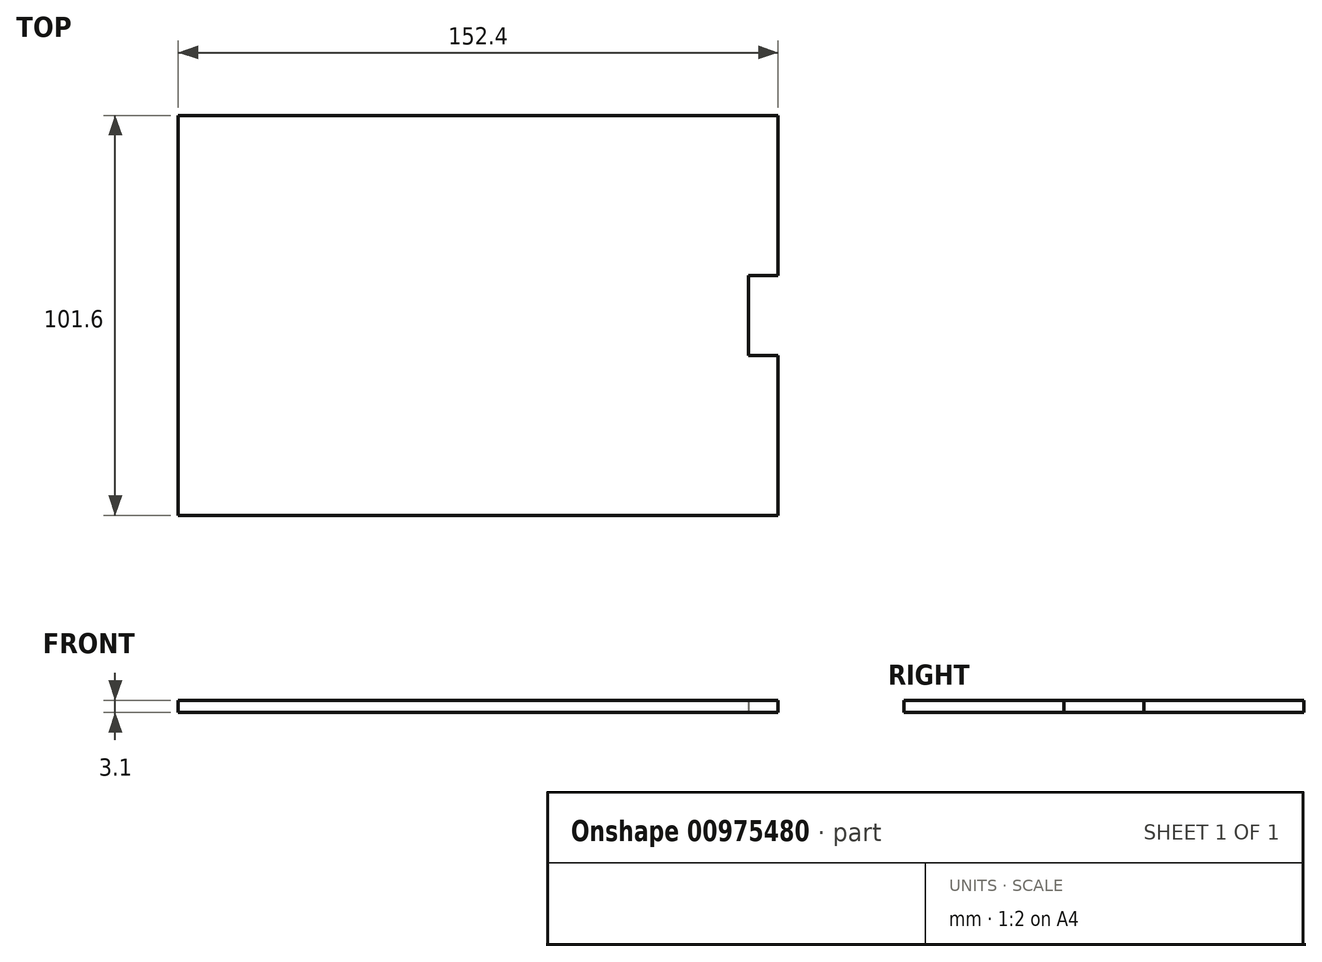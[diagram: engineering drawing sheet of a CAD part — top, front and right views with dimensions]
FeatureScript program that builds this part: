
annotation { "Feature Type Name" : "Feature", "Feature Type Description" : "" }
export const myFeature = defineFeature(function(context is Context, id is Id, definition is map)
    precondition{}
    {
        {
            var Q0;
            Q0=qCreatedBy(makeId("Top.planeOp"),FACE);
            var sketch = newSketch(context, id + "F0", { "sketchPlane" : qUnion([Q0])});
            skLineSegment(sketch, "E0.bottom", {"start": v(0, 0) * mm, "end": v(152.4, 0) * mm});
            skLineSegment(sketch, "E0.top", {"start": v(0, 101.6) * mm, "end": v(152.4, 101.6) * mm});
            skLineSegment(sketch, "E0.left", {"start": v(0, 0) * mm, "end": v(0, 101.6) * mm});
            skLineSegment(sketch, "E0.right", {"start": v(152.4, 0) * mm, "end": v(152.4, 101.6) * mm});
            skLineSegment(sketch, "E1.left", {"start": v(152.4, 60.96) * mm, "end": v(152.4, 40.64) * mm});
            skLineSegment(sketch, "E2", {"start": v(152.4, 50.8) * mm, "end": v(127.68, 50.8) * mm, "construction": true});
            skLineSegment(sketch, "E3.bottom", {"start": v(152.4, 60.96) * mm, "end": v(144.89, 60.96) * mm});
            skLineSegment(sketch, "E3.top", {"start": v(152.4, 40.64) * mm, "end": v(144.89, 40.64) * mm});
            skLineSegment(sketch, "E3.right", {"start": v(144.89, 60.96) * mm, "end": v(144.89, 40.64) * mm});
            skSolve(sketch);
        }
        {
            var Q0;
            Q0=makeQuery(id+"F0.imprint","IMPRINT",FACE,{"disambiguationData":[TD([[makeQuery(id+"F0.imprint","IMPRINT",EDGE,{"derivedFrom":sQuery(id+"F0.wireOp",EDGE,"E0.bottom")}),1.0]])]});
            var Q1;
            Q1=makeQuery(id+"F0.imprint","IMPRINT",FACE,{"disambiguationData":[TD([[makeQuery(id+"F0.imprint","IMPRINT",EDGE,{"derivedFrom":sQuery(id+"F0.wireOp",EDGE,"E1.bottom")}),-1.0]])]});
            extrude(context, id + "F1", {"entities" : qUnion([Q0, Q1]), "depth" : 3.1 * mm, "offsetDistance" : 25.4 * mm});
        }
    });
